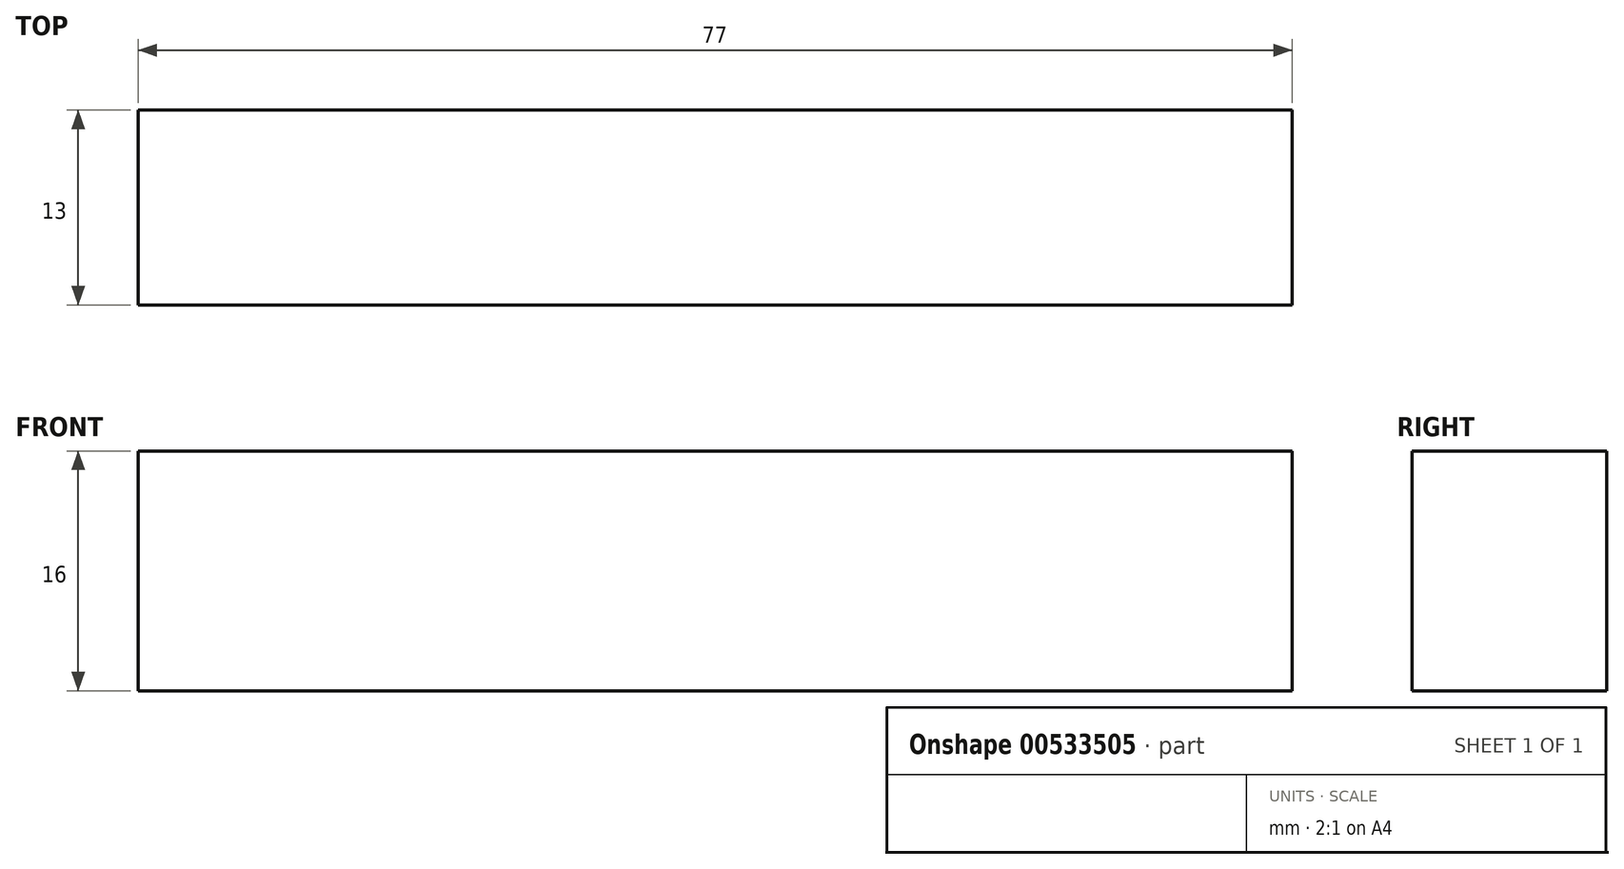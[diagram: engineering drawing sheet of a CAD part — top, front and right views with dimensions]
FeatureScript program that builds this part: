
annotation { "Feature Type Name" : "Feature", "Feature Type Description" : "" }
export const myFeature = defineFeature(function(context is Context, id is Id, definition is map)
    precondition{}
    {
        {
            var Q0;
            Q0=qCreatedBy(makeId("Top.planeOp"),FACE);
            var sketch = newSketch(context, id + "F0", { "sketchPlane" : qUnion([Q0])});
            skLineSegment(sketch, "E0.bottom", {"start": v(0, 0) * mm, "end": v(77, 0) * mm});
            skLineSegment(sketch, "E0.top", {"start": v(0, 13) * mm, "end": v(77, 13) * mm});
            skLineSegment(sketch, "E0.left", {"start": v(0, 0) * mm, "end": v(0, 13) * mm});
            skLineSegment(sketch, "E0.right", {"start": v(77, 0) * mm, "end": v(77, 13) * mm});
            skSolve(sketch);
        }
        {
            var Q0;
            Q0=qSketchRegion(id+"F0",true);
            extrude(context, id + "F1", {"entities" : qUnion([Q0]), "depth" : 16 * mm, "offsetDistance" : 25 * mm});
        }
    });
